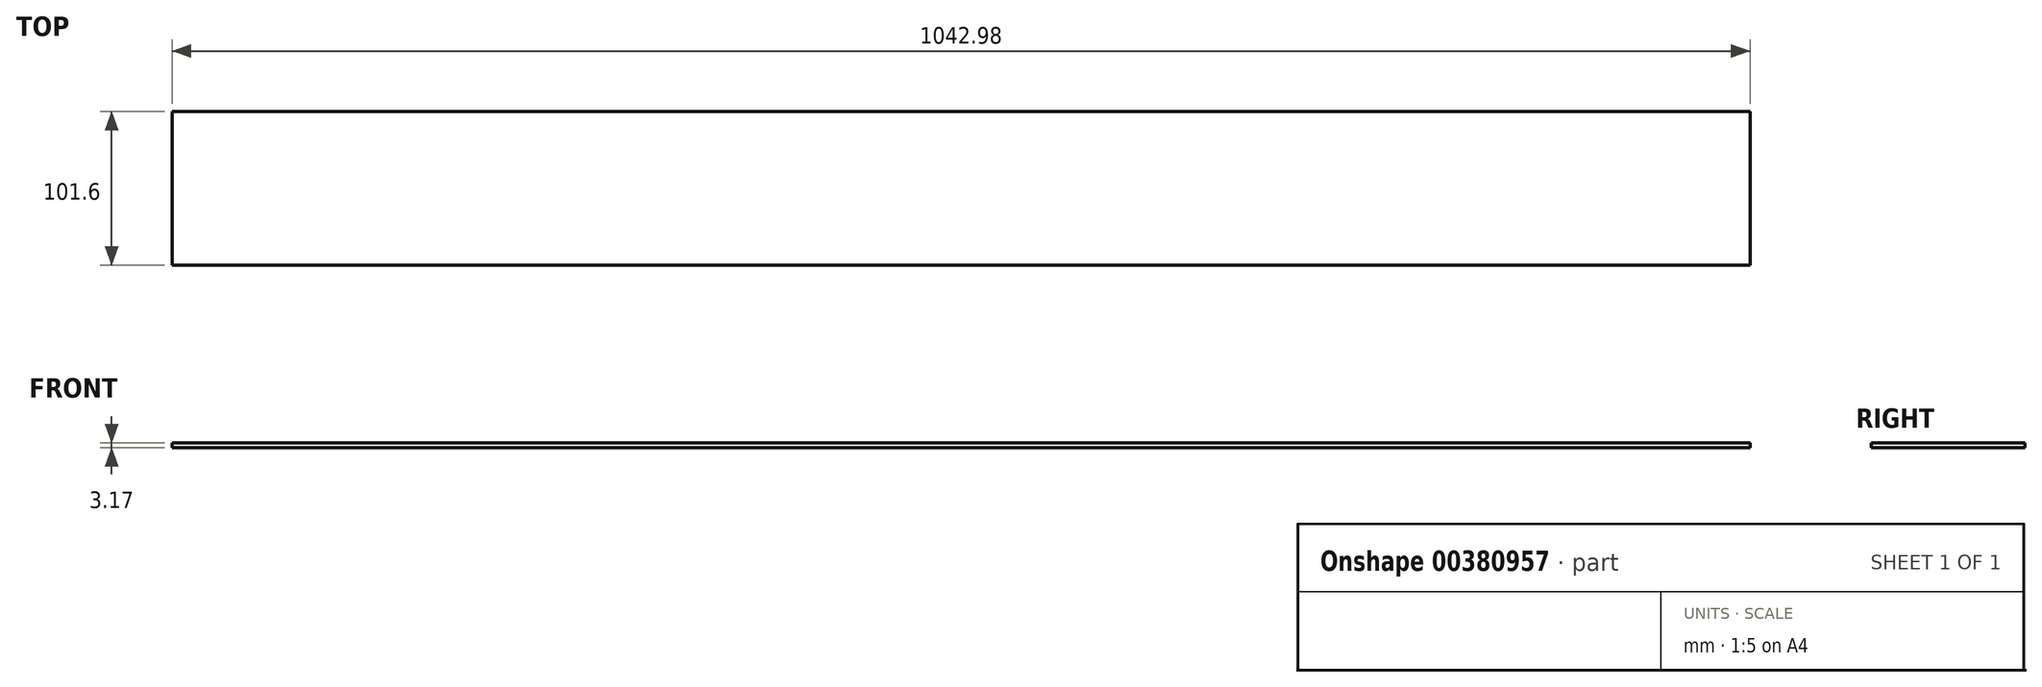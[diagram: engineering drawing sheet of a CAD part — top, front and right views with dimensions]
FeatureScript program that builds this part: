
annotation { "Feature Type Name" : "Feature", "Feature Type Description" : "" }
export const myFeature = defineFeature(function(context is Context, id is Id, definition is map)
    precondition{}
    {
        {
            var Q0;
            Q0=qCreatedBy(makeId("Top.planeOp"),FACE);
            var sketch = newSketch(context, id + "F0", { "sketchPlane" : qUnion([Q0])});
            skLineSegment(sketch, "E0.bottom", {"start": v(521.5, 50.8) * mm, "end": v(-521.5, 50.8) * mm});
            skLineSegment(sketch, "E0.top", {"start": v(521.5, -50.8) * mm, "end": v(-521.5, -50.8) * mm});
            skLineSegment(sketch, "E0.left", {"start": v(521.5, 50.8) * mm, "end": v(521.5, -50.8) * mm});
            skLineSegment(sketch, "E0.right", {"start": v(-521.5, 50.8) * mm, "end": v(-521.5, -50.8) * mm});
            skPoint(sketch, "E0.middle", {"position": v(0, 0) * mm});
            skSolve(sketch);
        }
        {
            var Q0;
            Q0=qSketchRegion(id+"F0",true);
            extrude(context, id + "F1", {"entities" : qUnion([Q0]), "depth" : 3.17 * mm});
        }
    });
